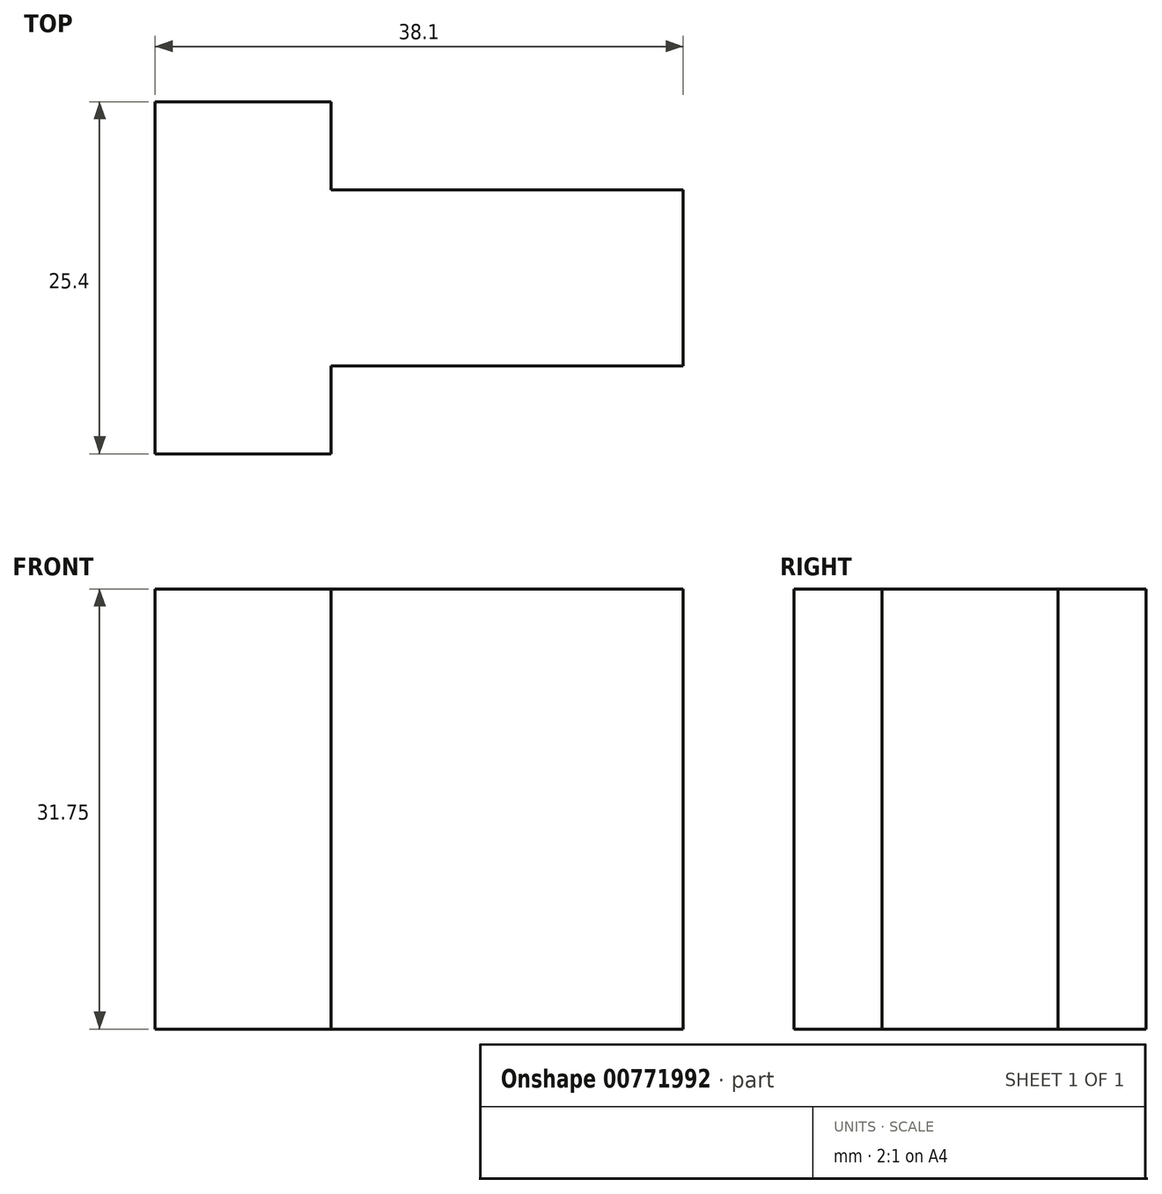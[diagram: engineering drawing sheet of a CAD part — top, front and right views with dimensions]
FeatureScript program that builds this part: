
annotation { "Feature Type Name" : "Feature", "Feature Type Description" : "" }
export const myFeature = defineFeature(function(context is Context, id is Id, definition is map)
    precondition{}
    {
        {
            var Q0;
            Q0=qCreatedBy(makeId("Top.planeOp"),FACE);
            var sketch = newSketch(context, id + "F0", { "sketchPlane" : qUnion([Q0])});
            skLineSegment(sketch, "E0", {"start": v(0, 0) * mm, "end": v(0, 25.4) * mm});
            skLineSegment(sketch, "E1", {"start": v(0, 25.4) * mm, "end": v(12.7, 25.4) * mm});
            skLineSegment(sketch, "E2", {"start": v(0, 0) * mm, "end": v(12.7, 0) * mm});
            skLineSegment(sketch, "E3", {"start": v(12.7, 0) * mm, "end": v(12.7, 6.35) * mm});
            skLineSegment(sketch, "E4", {"start": v(12.7, 25.4) * mm, "end": v(12.7, 19.05) * mm});
            skLineSegment(sketch, "E5", {"start": v(12.7, 6.35) * mm, "end": v(38.1, 6.35) * mm});
            skLineSegment(sketch, "E6", {"start": v(12.7, 19.05) * mm, "end": v(38.1, 19.05) * mm});
            skLineSegment(sketch, "E7", {"start": v(38.1, 19.05) * mm, "end": v(38.1, 6.35) * mm});
            skSolve(sketch);
        }
        {
            var Q0;
            Q0=makeQuery(id+"F0.imprint","IMPRINT",FACE,{"disambiguationData":[TD([[makeQuery(id+"F0.imprint","IMPRINT",EDGE,{"derivedFrom":sQuery(id+"F0.wireOp",EDGE,"E0")}),-1.0]])]});
            extrude(context, id + "F1", {"entities" : qUnion([Q0]), "depth" : 31.75 * mm, "offsetDistance" : 25.4 * mm});
        }
    });
